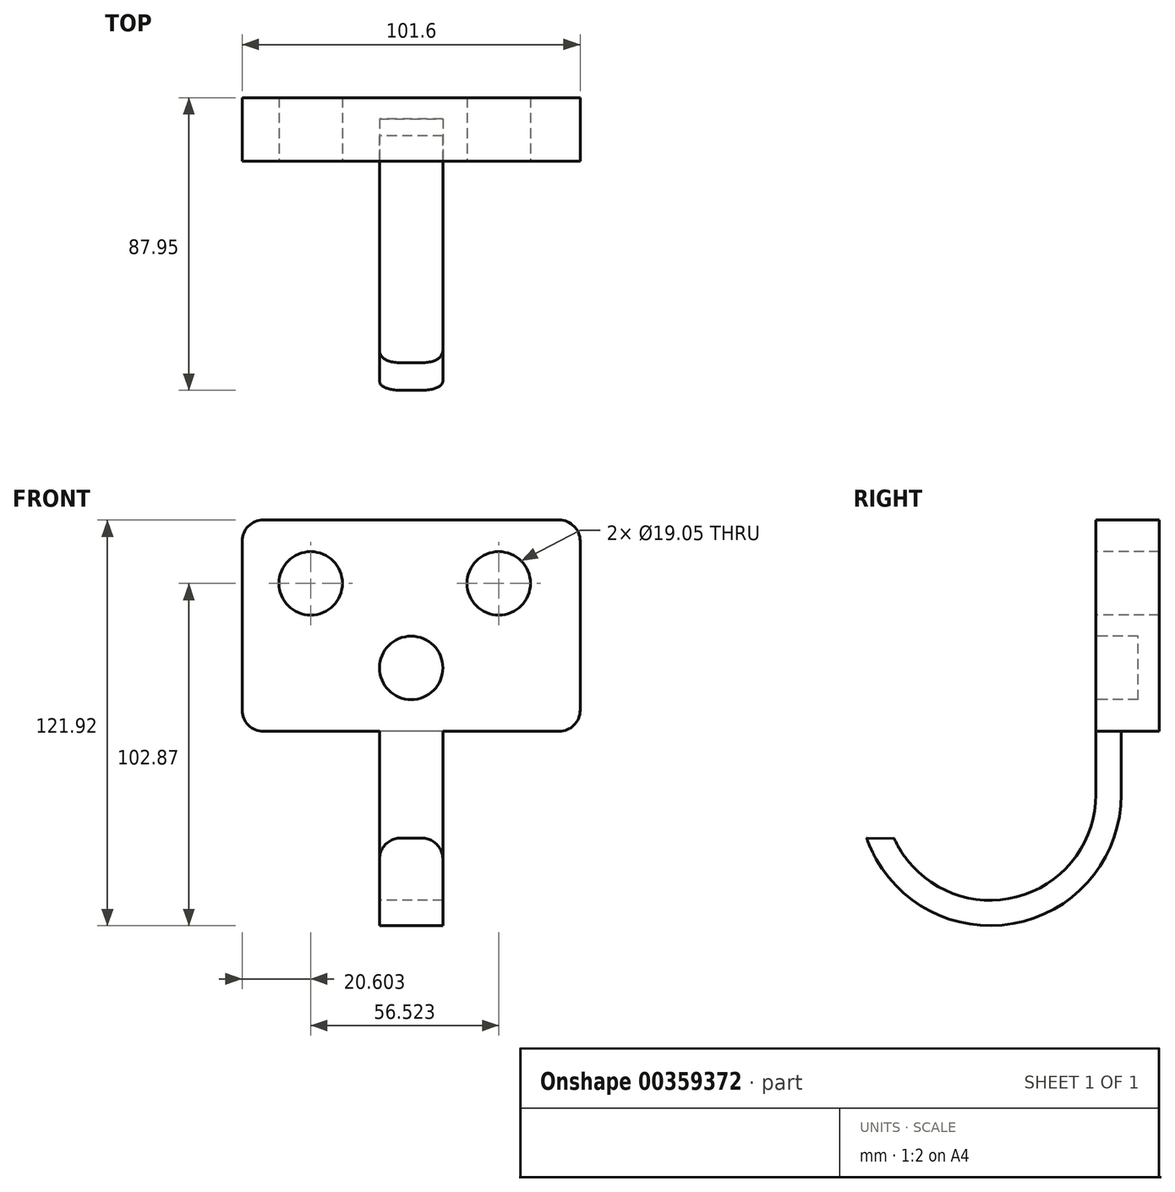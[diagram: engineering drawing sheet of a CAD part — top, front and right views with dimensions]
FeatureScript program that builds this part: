
annotation { "Feature Type Name" : "Feature", "Feature Type Description" : "" }
export const myFeature = defineFeature(function(context is Context, id is Id, definition is map)
    precondition{}
    {
        {
            var Q0;
            Q0=qCreatedBy(makeId("Right.planeOp"),FACE);
            var sketch = newSketch(context, id + "F0", { "sketchPlane" : qUnion([Q0])});
            skLineSegment(sketch, "E0.bottom", {"start": v(0, 0) * mm, "end": v(19.05, 0) * mm});
            skLineSegment(sketch, "E0.top", {"start": v(0, 63.5) * mm, "end": v(19.05, 63.5) * mm});
            skLineSegment(sketch, "E0.left", {"start": v(0, 0) * mm, "end": v(0, 63.5) * mm});
            skLineSegment(sketch, "E0.right", {"start": v(19.05, 0) * mm, "end": v(19.05, 63.5) * mm});
            skLineSegment(sketch, "E1.bottom", {"start": v(0, 0) * mm, "end": v(7.62, 0) * mm});
            skLineSegment(sketch, "E1.top", {"start": v(0, -19.05) * mm, "end": v(7.62, -19.05) * mm});
            skLineSegment(sketch, "E1.left", {"start": v(0, 0) * mm, "end": v(0, -19.05) * mm});
            skLineSegment(sketch, "E1.right", {"start": v(7.62, 0) * mm, "end": v(7.62, -19.05) * mm});
            skArc(sketch, "E2", {"start": v(7.62, -19.05) * mm, "mid": v(-25.14, -57.86) * mm, "end": v(-68.9, -32.08) * mm});
            skLineSegment(sketch, "E3", {"start": v(0, -19.05) * mm, "end": v(-76.36, -19.05) * mm});
            skArc(sketch, "E4", {"start": v(0, -19.05) * mm, "mid": v(-25.02, -50.08) * mm, "end": v(-60.64, -32.21) * mm});
            skLineSegment(sketch, "E5", {"start": v(-60.64, -32.21) * mm, "end": v(-68.9, -32.08) * mm});
            skSolve(sketch);
        }
        {
            var Q0;
            Q0=makeQuery(id+"F0.imprint","IMPRINT",FACE,{"disambiguationData":[TD([[makeQuery(id+"F0.imprint","IMPRINT",EDGE,{"derivedFrom":sQuery(id+"F0.wireOp",EDGE,"E0.bottom")}),1.0]])]});
            extrude(context, id + "F1", {"entities" : qUnion([Q0]), "endBound" : BoundingType.SYMMETRIC, "depth" : 101.6 * mm});
        }
        {
            var Q0;
            Q0 = qSketchRegion(id + "F0", true);
            extrude(context, id + "F2", {"entities" : qUnion([Q0]), "operationType" : NewBodyOperationType.ADD, "endBound" : BoundingType.SYMMETRIC, "depth" : 19.05 * mm});
        }
        {
            var Q0;
            Q0=makeQuery(id+"F2.opExtrude","CAP_EDGE",EDGE,{"disambiguationData":[OSD([sQuery(id+"F0.wireOp",EDGE,"E5")])],"isStart":false});
            var Q1;
            Q1=makeQuery(id+"F2.opExtrude","CAP_EDGE",EDGE,{"disambiguationData":[OSD([sQuery(id+"F0.wireOp",EDGE,"E5")])],"isStart":true});
            var Q2;
            Q2=makeQuery(id+"F1.opExtrude","CAP_EDGE",EDGE,{"disambiguationData":[OSD([sQuery(id+"F0.wireOp",EDGE,"E0.bottom"),sQuery(id+"F0.wireOp",EDGE,"E1.bottom")])],"isStart":false});
            var Q3;
            Q3=makeQuery(id+"F1.opExtrude","CAP_EDGE",EDGE,{"disambiguationData":[OSD([sQuery(id+"F0.wireOp",EDGE,"E0.top")])],"isStart":false});
            var Q4;
            Q4=makeQuery(id+"F1.opExtrude","CAP_EDGE",EDGE,{"disambiguationData":[OSD([sQuery(id+"F0.wireOp",EDGE,"E0.top")])],"isStart":true});
            var Q5;
            Q5=makeQuery(id+"F1.opExtrude","CAP_EDGE",EDGE,{"disambiguationData":[OSD([sQuery(id+"F0.wireOp",EDGE,"E0.bottom"),sQuery(id+"F0.wireOp",EDGE,"E1.bottom")])],"isStart":true});
            fillet(context, id + "F3", {"entities" : qUnion([Q0, Q1, Q2, Q3, Q4, Q5]), "radius" : 6.35 * mm, "tangentPropagation" : true, "allowEdgeOverflow" : false});
        }
        {
            var Q0;
            {var subQ0=sQuery(id+"F0.wireOp",EDGE,"E0.left");Q0=makeQuery(id+"F2.boolean.opBoolean","MERGE",FACE,{"derivedFrom":[makeQuery(id+"F1.opExtrude","SWEPT_FACE",FACE,{"disambiguationData":[OSD([subQ0])]}),makeQuery(id+"F2.opExtrude","SWEPT_FACE",FACE,{"disambiguationData":[OSD([subQ0,sQuery(id+"F0.wireOp",EDGE,"E1.left")])]})]});}
            var sketch = newSketch(context, id + "F4", { "sketchPlane" : qUnion([Q0])});
            skCircle(sketch, "E6", {"center": v(-30.2, 44.45) * mm, "radius": 9.53 * mm});
            skCircle(sketch, "E7", {"center": v(26.33, 44.45) * mm, "radius": 9.53 * mm});
            skCircle(sketch, "E8", {"center": v(0, 19.05) * mm, "radius": 9.53 * mm});
            skLineSegment(sketch, "E9", {"start": v(-30.2, 44.45) * mm, "end": v(26.33, 44.45) * mm});
            skSolve(sketch);
        }
        {
            var Q0;
            Q0=makeQuery(id+"F4.imprint","IMPRINT",FACE,{"disambiguationData":[TD([[makeQuery(id+"F4.imprint","IMPRINT",EDGE,{"derivedFrom":sQuery(id+"F4.wireOp",EDGE,"E6")}),1.0]])]});
            var Q1;
            Q1=makeQuery(id+"F4.imprint","IMPRINT",FACE,{"disambiguationData":[TD([[makeQuery(id+"F4.imprint","IMPRINT",EDGE,{"derivedFrom":sQuery(id+"F4.wireOp",EDGE,"E7")}),1.0]])]});
            extrude(context, id + "F5", {"entities" : qUnion([Q0, Q1]), "operationType" : NewBodyOperationType.REMOVE, "oppositeDirection" : true, "depth" : 25.4 * mm});
        }
        {
            var Q0;
            Q0 = qSketchRegion(id + "F4", true);
            extrude(context, id + "F6", {"entities" : qUnion([Q0]), "operationType" : NewBodyOperationType.REMOVE, "oppositeDirection" : true, "depth" : 12.7 * mm});
        }
    });
